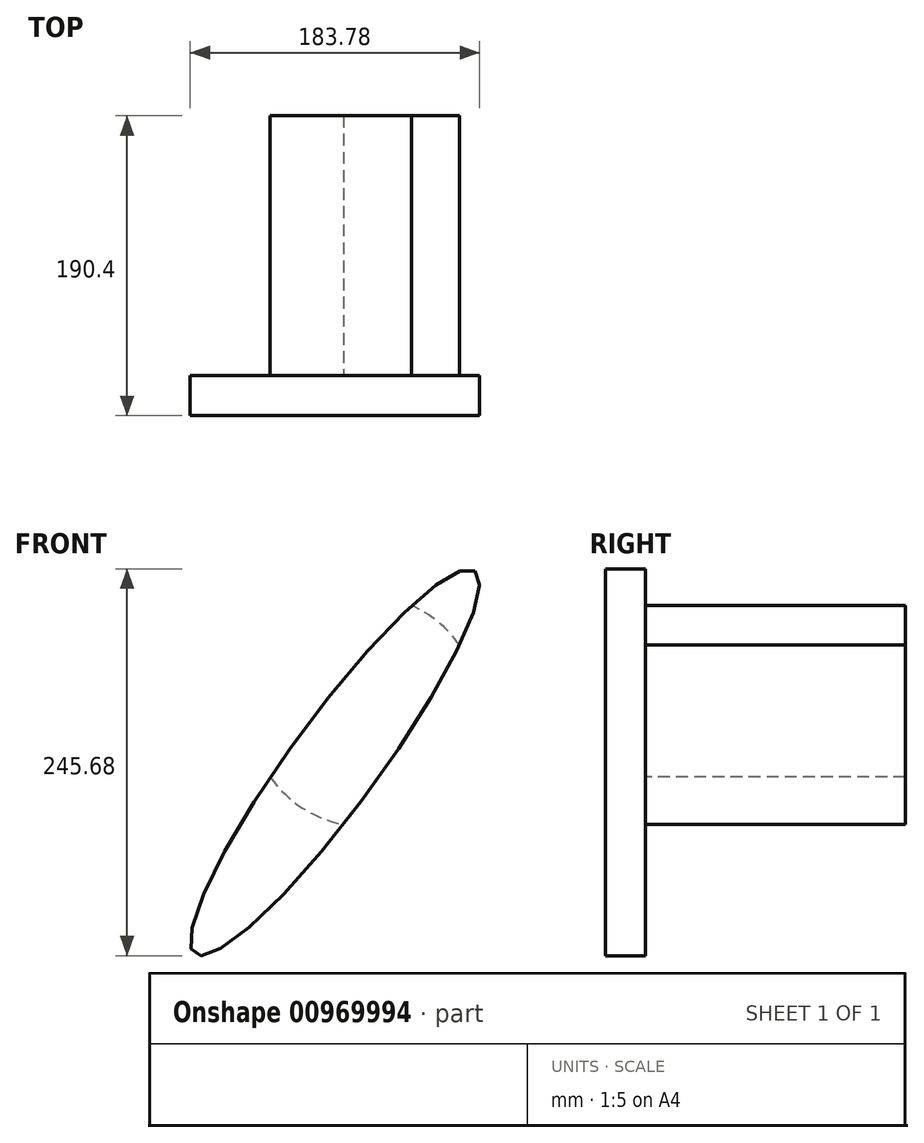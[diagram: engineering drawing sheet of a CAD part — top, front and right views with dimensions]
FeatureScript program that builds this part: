
annotation { "Feature Type Name" : "Feature", "Feature Type Description" : "" }
export const myFeature = defineFeature(function(context is Context, id is Id, definition is map)
    precondition{}
    {
        {
            var Q0;
            Q0=qCreatedBy(makeId("Front.planeOp"),FACE);
            var sketch = newSketch(context, id + "F0", { "sketchPlane" : qUnion([Q0])});
            skEllipse(sketch, "E0", {"center": v(0, 0) * mm, "majorRadius": 150.78 * mm, "minorRadius": 28.25 * mm, "majorAxis": v(0.6, 0.8)});
            skSolve(sketch);
        }
        {
            var Q0;
            Q0=makeQuery(id+"F0.imprint","IMPRINT",FACE,{"disambiguationData":[TD([[makeQuery(id+"F0.imprint","IMPRINT",EDGE,{"derivedFrom":sQuery(id+"F0.wireOp",EDGE,"E0")}),1.0]])]});
            var Q1;
            Q1=sQuery(id+"F0.wireOp",EDGE,"E0");
            extrude(context, id + "F1", {"entities" : qUnion([Q0]), "surfaceEntities" : qUnion([Q1]), "depth" : 25.4 * mm, "offsetDistance" : 25.4 * mm});
        }
        {
            var Q0;
            Q0=makeQuery(id+"F1.opExtrude","CAP_FACE",FACE,{"disambiguationData":[OSD([sQuery(id+"F0.wireOp",EDGE,"E0")])],"isStart":true});
            var sketch = newSketch(context, id + "F2", { "sketchPlane" : qUnion([Q0])});
            skCircle(sketch, "E1", {"center": v(-19.1, 32.57) * mm, "radius": 73.29 * mm});
            skSolve(sketch);
        }
        {
            var Q0;
            {var subQ0=sQuery(id+"F2.wireOp",EDGE,"E1");var subQ1=makeQuery(id+"F1.opExtrude","CAP_EDGE",EDGE,{"disambiguationData":[OSD([sQuery(id+"F0.wireOp",EDGE,"E0")])],"isStart":true});var subQ2=makeQuery(id+"F2.imprint","INTERSECT",VERTEX,{"disambiguationData":[OD(0.0)],"derivedFrom":[subQ1,subQ0]});Q0=makeQuery(id+"F2.imprint","IMPRINT",FACE,{"disambiguationData":[TD([[makeQuery(id+"F2.imprint","IMPRINT",EDGE,{"disambiguationData":[TD([[subQ2,1.0]])],"derivedFrom":subQ0}),1.0]])]});}
            var Q1;
            Q1=sQuery(id+"F2.wireOp",EDGE,"E1");
            extrude(context, id + "F3", {"entities" : qUnion([Q0]), "surfaceEntities" : qUnion([Q1]), "depth" : 165 * mm, "offsetDistance" : 25.4 * mm});
        }
    });
